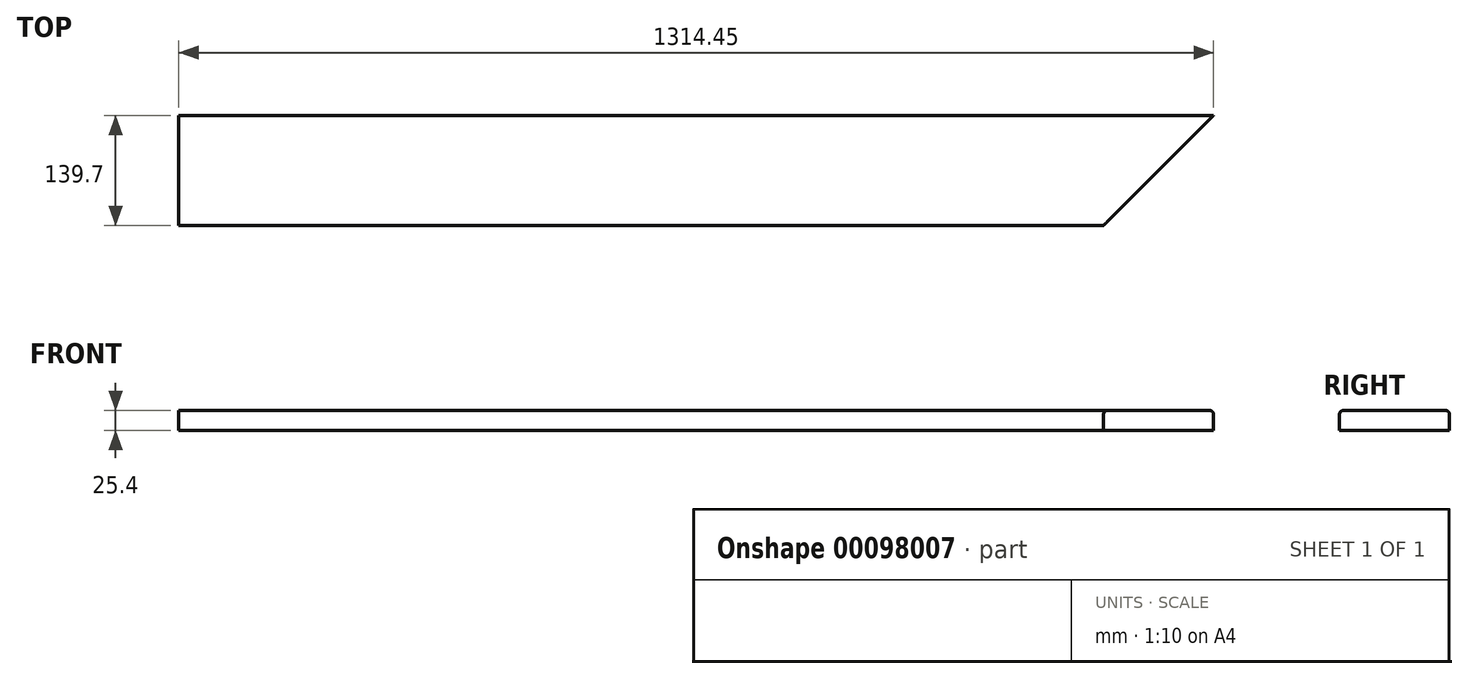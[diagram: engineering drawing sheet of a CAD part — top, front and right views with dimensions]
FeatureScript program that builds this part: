
annotation { "Feature Type Name" : "Feature", "Feature Type Description" : "" }
export const myFeature = defineFeature(function(context is Context, id is Id, definition is map)
    precondition{}
    {
        {
            var Q0;
            Q0=qCreatedBy(makeId("Top.planeOp"),FACE);
            var sketch = newSketch(context, id + "F0", { "sketchPlane" : qUnion([Q0])});
            skLineSegment(sketch, "E0", {"start": v(0, 0) * mm, "end": v(1174.75, 0) * mm});
            skLineSegment(sketch, "E1", {"start": v(0, 0) * mm, "end": v(0, 139.7) * mm});
            skLineSegment(sketch, "E2", {"start": v(0, 139.7) * mm, "end": v(1314.45, 139.7) * mm});
            skLineSegment(sketch, "E3", {"start": v(1174.75, 0) * mm, "end": v(1314.45, 139.7) * mm});
            skSolve(sketch);
        }
        {
            var Q0;
            Q0=makeQuery(id+"F0.imprint","IMPRINT",FACE,{"disambiguationData":[TD([[makeQuery(id+"F0.imprint","IMPRINT",EDGE,{"derivedFrom":sQuery(id+"F0.wireOp",EDGE,"E0")}),1.0]])]});
            extrude(context, id + "F1", {"entities" : qUnion([Q0]), "depth" : 25.4 * mm});
        }
        {
            var Q0;
            Q0=makeQuery(id+"F1.opExtrude","CAP_EDGE",EDGE,{"disambiguationData":[OSD([sQuery(id+"F0.wireOp",EDGE,"E0")])],"isStart":false});
            var Q1;
            Q1=makeQuery(id+"F1.opExtrude","CAP_EDGE",EDGE,{"disambiguationData":[OSD([sQuery(id+"F0.wireOp",EDGE,"E2")])],"isStart":false});
            fillet(context, id + "F2", {"entities" : qUnion([Q0, Q1]), "radius" : 5.08 * mm, "tangentPropagation" : true, "allowEdgeOverflow" : false});
        }
    });
